# Revit family: РИДАН_FVR-R_Фильтр сетчатый с пробкой
name_source: partatom
category: Арматура трубопроводов
units: mm (PartAtom-declared; Revit-internal decimal feet)

## family parameters
Всегда вертикально = Да
На основе рабочей плоскости = Нет
Общий = Нет
При загрузке вырезать с полостями = Нет
Размер круглого соединителя = Использовать диаметр
Тип детали = Вставляется

## types (6) — shared parameters
ADSK_Версия Revit = 2019
ADSK_Версия семейства = 1.0
ADSK_Единица измерения = шт.
ADSK_Завод-изготовитель = ООО «Ридан-Трейд»
ADSK_Количество = 1
ADSK_Материал = Латунь корпус
ADSK_Расход жидкости = 0 м³/ч
LT = FVR-R
URL = https://ridan.ru

## per-type parameters (varying)
- DN15: ADSK_Диаметр условный=15 мм; ADSK_Код изделия=065B8341R; ADSK_Марка=FVR-DR DN15; ADSK_Масса=0.278; ADSK_Наименование=Фильтр сетчатый с пробкой FVR-R PN25, Tmax=130C, DN15; a=18 мм; a1=8 мм; ang1=45.00°; b=2 мм; b1=7 мм; c=1 мм; c1=6 мм; d=10 мм; d1=24 мм; e=1 мм; e1=11 мм; f=3 мм; f1=1 мм; g=15 мм; g1=14 мм; h=12 мм; h1=13 мм; i=22 мм; i1=15 мм; j=20 мм; j1=25 мм; k=25 мм; k1=5 мм; l=19 мм; m=31 мм
- DN20: ADSK_Диаметр условный=20 мм; ADSK_Код изделия=065B8342R; ADSK_Марка=FVR-DR DN20; ADSK_Масса=0.391; ADSK_Наименование=Фильтр сетчатый с пробкой FVR-R PN25, Tmax=130C, DN20; a=20 мм; a1=7 мм; ang1=45.00°; b=3 мм; b1=10 мм; c=0 мм; c1=7 мм; d=13 мм; d1=32 мм; e=3 мм; e1=13 мм; f=4 мм; f1=2 мм; g=20 мм; g1=17 мм; h=13 мм; h1=16 мм; i=29 мм; i1=18 мм; j=26 мм; j1=25 мм; k=31 мм; k1=2 мм; l=25 мм; m=41 мм
- DN25: ADSK_Диаметр условный=25 мм; ADSK_Код изделия=065B8343R; ADSK_Марка=FVR-DR DN25; ADSK_Масса=0.557; ADSK_Наименование=Фильтр сетчатый с пробкой FVR-R PN25, Tmax=130C, DN25; a=24 мм; a1=7 мм; ang1=45.00°; b=3 мм; b1=10 мм; c=1 мм; c1=7 мм; d=16 мм; d1=31 мм; e=3 мм; e1=14 мм; f=4 мм; f1=2 мм; g=24 мм; g1=17 мм; h=15 мм; h1=16 мм; i=34 мм; i1=18 мм; j=30 мм; j1=25 мм; k=37 мм; k1=6 мм; l=31 мм; m=49 мм
- DN32: ADSK_Диаметр условный=32 мм; ADSK_Код изделия=065B8344R; ADSK_Марка=FVR-DR DN32; ADSK_Масса=0.746; ADSK_Наименование=Фильтр сетчатый с пробкой FVR-R PN25, Tmax=130C, DN32; a=25 мм; a1=9 мм; ang1=45.00°; b=3 мм; b1=8 мм; c=1 мм; c1=11 мм; d=14 мм; d1=40 мм; e=8 мм; e1=19 мм; f=4 мм; f1=2 мм; g=30 мм; g1=23 мм; h=24 мм; h1=21 мм; i=44 мм; i1=25 мм; j=40 мм; j1=37 мм; k=47 мм; k1=7 мм; l=39 мм; m=54 мм
- DN40: ADSK_Диаметр условный=40 мм; ADSK_Код изделия=065B8345R; ADSK_Марка=FVR-DR DN40; ADSK_Масса=1.114; ADSK_Наименование=Фильтр сетчатый с пробкой FVR-R PN25, Tmax=130C, DN40; a=27 мм; a1=10 мм; ang1=45.00°; b=5 мм; b1=8 мм; c=0 мм; c1=11 мм; d=9 мм; d1=49 мм; e=17 мм; e1=21 мм; f=4 мм; f1=2 мм; g=30 мм; g1=25 мм; h=23 мм; h1=24 мм; i=50 мм; i1=27 мм; j=47 мм; j1=39 мм; k=54 мм; k1=9 мм; l=45 мм; m=64 мм
- DN50: ADSK_Диаметр условный=50 мм; ADSK_Код изделия=065B8346R; ADSK_Марка=FVR-DR DN50; ADSK_Масса=1.71; ADSK_Наименование=Фильтр сетчатый с пробкой FVR-R PN25, Tmax=130C, DN50; a=32 мм; a1=12 мм; ang1=46.00°; b=4 мм; b1=9 мм; c=1 мм; c1=14 мм; d=15 мм; d1=58 мм; e=20 мм; e1=26 мм; f=4 мм; f1=5 мм; g=39 мм; g1=33 мм; h=29 мм; h1=31 мм; i=64 мм; i1=35 мм; j=58 мм; j1=46 мм; k=68 мм; k1=10 мм; l=58 мм; m=82 мм
